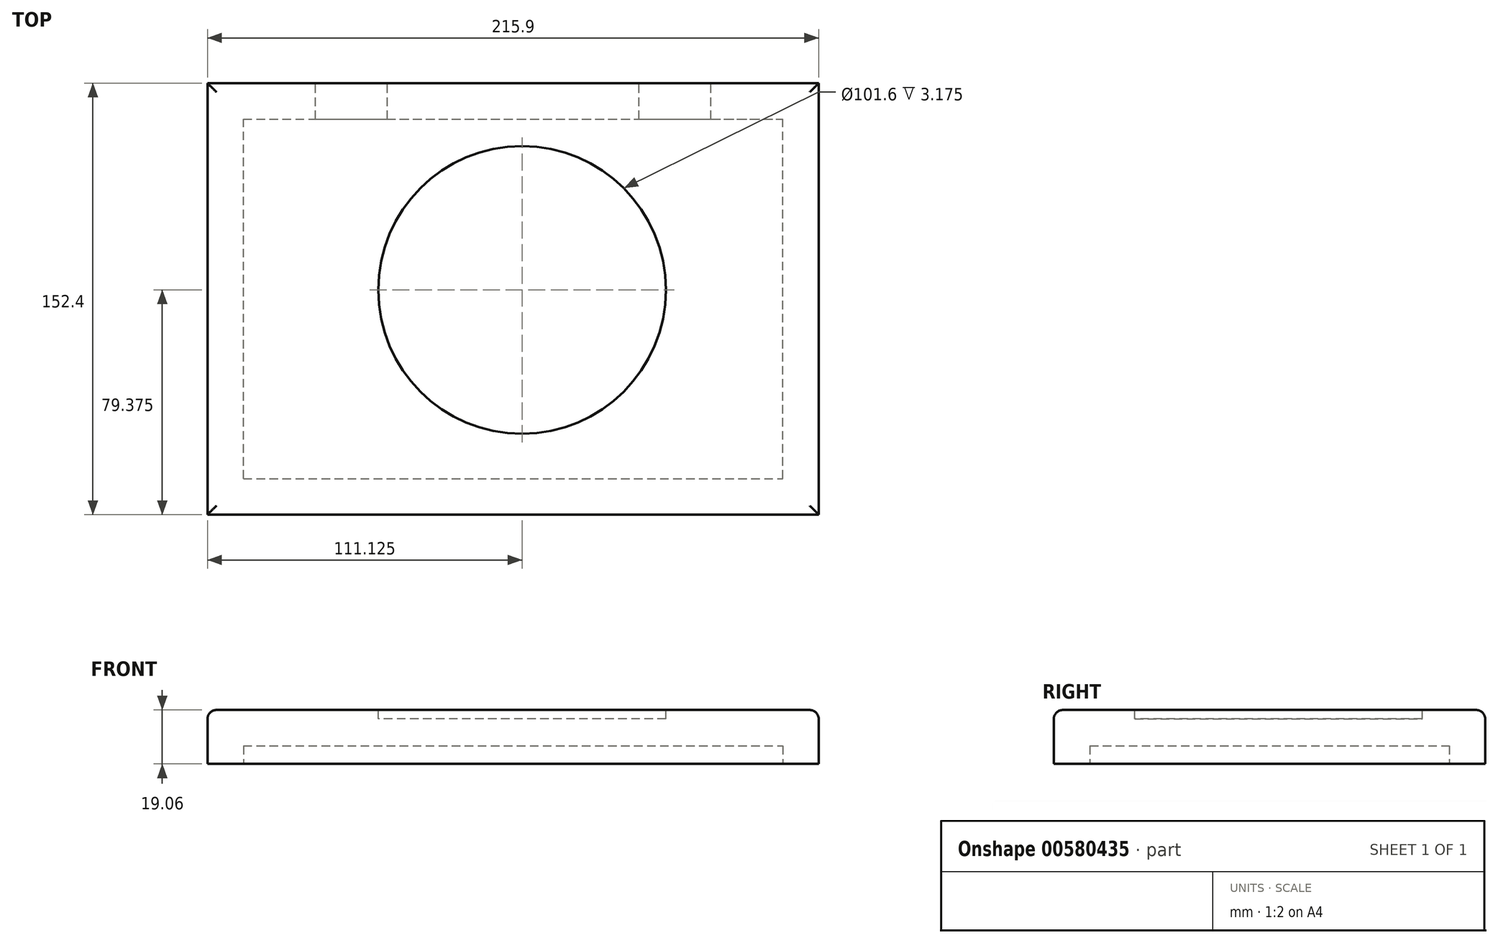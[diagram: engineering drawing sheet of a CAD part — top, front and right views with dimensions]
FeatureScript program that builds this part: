
annotation { "Feature Type Name" : "Feature", "Feature Type Description" : "" }
export const myFeature = defineFeature(function(context is Context, id is Id, definition is map)
    precondition{}
    {
        {
            var Q0;
            Q0=qCreatedBy(makeId("Front.planeOp"),FACE);
            var sketch = newSketch(context, id + "F0", { "sketchPlane" : qUnion([Q0])});
            skLineSegment(sketch, "E0.bottom", {"start": v(-107.95, 9.53) * mm, "end": v(107.95, 9.53) * mm});
            skLineSegment(sketch, "E0.top", {"start": v(-107.95, -9.52) * mm, "end": v(107.95, -9.52) * mm});
            skLineSegment(sketch, "E0.left", {"start": v(-107.95, 9.53) * mm, "end": v(-107.95, -9.52) * mm});
            skLineSegment(sketch, "E0.right", {"start": v(107.95, 9.53) * mm, "end": v(107.95, -9.52) * mm});
            skPoint(sketch, "E0.middle", {"position": v(0, 0) * mm});
            skSolve(sketch);
        }
        {
            var Q0;
            Q0 = qSketchRegion(id + "F0", true);
            extrude(context, id + "F1", {"entities" : qUnion([Q0]), "depth" : 152.4 * mm, "offsetDistance" : 25.4 * mm});
        }
        {
            var Q0;
            Q0=makeQuery(id+"F1.opExtrude","SWEPT_FACE",FACE,{"disambiguationData":[OSD([sQuery(id+"F0.wireOp",EDGE,"E0.top")])]});
            var sketch = newSketch(context, id + "F2", { "sketchPlane" : qUnion([Q0])});
            skLineSegment(sketch, "E1.bottom", {"start": v(-95.25, 139.7) * mm, "end": v(95.25, 139.7) * mm});
            skLineSegment(sketch, "E1.top", {"start": v(-95.25, 12.7) * mm, "end": v(95.25, 12.7) * mm});
            skLineSegment(sketch, "E1.left", {"start": v(-95.25, 139.7) * mm, "end": v(-95.25, 12.7) * mm});
            skLineSegment(sketch, "E1.right", {"start": v(95.25, 139.7) * mm, "end": v(95.25, 12.7) * mm});
            skSolve(sketch);
        }
        {
            var Q0;
            Q0 = qSketchRegion(id + "F2", true);
            extrude(context, id + "F3", {"entities" : qUnion([Q0]), "operationType" : NewBodyOperationType.REMOVE, "oppositeDirection" : true, "depth" : 6.35 * mm, "offsetDistance" : 25.4 * mm});
        }
        {
            var Q0;
            Q0=makeQuery(id+"F1.opExtrude","SWEPT_FACE",FACE,{"disambiguationData":[OSD([sQuery(id+"F0.wireOp",EDGE,"E0.top")])]});
            var sketch = newSketch(context, id + "F4", { "sketchPlane" : qUnion([Q0])});
            skLineSegment(sketch, "E2.bottom", {"start": v(-69.85, 12.7) * mm, "end": v(-44.45, 12.7) * mm});
            skLineSegment(sketch, "E2.top", {"start": v(-69.85, 0) * mm, "end": v(-44.45, 0) * mm});
            skLineSegment(sketch, "E2.left", {"start": v(-69.85, 12.7) * mm, "end": v(-69.85, 0) * mm});
            skLineSegment(sketch, "E2.right", {"start": v(-44.45, 12.7) * mm, "end": v(-44.45, 0) * mm});
            skPoint(sketch, "E3.oppositeSnap0", {"position": v(-57.15, 0) * mm});
            skLineSegment(sketch, "E3.bottom", {"start": v(44.45, 12.7) * mm, "end": v(69.85, 12.7) * mm});
            skLineSegment(sketch, "E3.top", {"start": v(44.45, 0) * mm, "end": v(69.85, 0) * mm});
            skLineSegment(sketch, "E3.left", {"start": v(44.45, 12.7) * mm, "end": v(44.45, 0) * mm});
            skLineSegment(sketch, "E3.right", {"start": v(69.85, 12.7) * mm, "end": v(69.85, 0) * mm});
            skSolve(sketch);
        }
        {
            var Q0;
            Q0 = qSketchRegion(id + "F4", true);
            extrude(context, id + "F5", {"entities" : qUnion([Q0]), "operationType" : NewBodyOperationType.REMOVE, "oppositeDirection" : true, "depth" : 0.16 * mm, "offsetDistance" : 25.4 * mm});
        }
        {
            var Q0;
            Q0=makeQuery(id+"F1.opExtrude","SWEPT_FACE",FACE,{"disambiguationData":[OSD([sQuery(id+"F0.wireOp",EDGE,"E0.bottom")])]});
            fillet(context, id + "F6", {"entities" : qUnion([Q0]), "radius" : 3.17 * mm, "tangentPropagation" : true, "allowEdgeOverflow" : false});
        }
        {
            var Q0;
            Q0=makeQuery(id+"F1.opExtrude","SWEPT_FACE",FACE,{"disambiguationData":[OSD([sQuery(id+"F0.wireOp",EDGE,"E0.bottom")])]});
            var sketch = newSketch(context, id + "F7", { "sketchPlane" : qUnion([Q0])});
            skCircle(sketch, "E4", {"center": v(3.17, -73.02) * mm, "radius": 50.8 * mm});
            skSolve(sketch);
        }
        {
            var Q0;
            Q0 = qSketchRegion(id + "F7", true);
            extrude(context, id + "F8", {"entities" : qUnion([Q0]), "operationType" : NewBodyOperationType.REMOVE, "oppositeDirection" : true, "depth" : 3.17 * mm, "offsetDistance" : 25.4 * mm});
        }
    });
